FCSTD DOCUMENT  (FreeCAD 0.18R4 (GitTag))
Label: ZAntiWobbler
License: All rights reserved
LicenseURL: http://en.wikipedia.org/wiki/All_rights_reserved
objects: Sketcher::SketchObject×1, Spreadsheet::Sheet×1
note: 1 computed .brp shape members not serialized (recipe doc carries the construction recipe); baked Part::Feature solids carry a one-line shape summary decoded from their .brp

FEATURE [Sketcher::SketchObject] Sketch
  expr: Constraints[35] = Parameters.AntiWobblerRadius - Parameters.AntiWobblerRadiusToCut + 3mm
  expr: Constraints[34] = Parameters.AntiWobblerRadius * 2
  expr: Constraints[6] = Parameters.M3ThreadRadius
  expr: Constraints[14] = Parameters.M3ThreadRadius
  expr: Constraints[13] = Parameters.M3HeadRadius
  expr: Constraints[7] = Parameters.AntiWobblerRadiusToCut
  expr: Constraints[1] = Parameters.AntiWobblerRadius
  expr: Constraints[8] = Parameters.M3HeadRadius
  expr: Constraints[20] = Parameters.M3ThreadRadius
  expr: Constraints[15] = Parameters.AntiWobblerScrewSeparation
  expr: Constraints[10] = Parameters.M3HeadRadius
  expr: Constraints[5] = Parameters.M3HeadRadius
  expr: Constraints[2] = Parameters.ZScrewRadiusWithStopScrew
  expr: Constraints[11] = Parameters.M3ThreadRadius
  sketch-geometry (16):
    g0: Circle CenterX=0 CenterY=0 CenterZ=0 NormalX=0 NormalY=0 NormalZ=1 AngleXU=0 Radius=11
    g1: Circle CenterX=0 CenterY=0 CenterZ=0 NormalX=0 NormalY=0 NormalZ=1 AngleXU=0 Radius=5
    g2: Circle CenterX=5.65685 CenterY=5.65685 CenterZ=0 NormalX=0 NormalY=0 NormalZ=1 AngleXU=0 Radius=2
    g3: Circle CenterX=5.65685 CenterY=5.65685 CenterZ=0 NormalX=0 NormalY=0 NormalZ=1 AngleXU=0 Radius=3
    g4: Circle CenterX=5.65685 CenterY=-5.65685 CenterZ=0 NormalX=0 NormalY=0 NormalZ=1 AngleXU=0 Radius=3
    g5: Circle CenterX=-5.65685 CenterY=-5.65685 CenterZ=0 NormalX=0 NormalY=0 NormalZ=1 AngleXU=0 Radius=3
    g6: Circle CenterX=-5.65685 CenterY=-5.65685 CenterZ=0 NormalX=0 NormalY=0 NormalZ=1 AngleXU=0 Radius=2
    g7: Circle CenterX=-5.65685 CenterY=5.65685 CenterZ=0 NormalX=0 NormalY=0 NormalZ=1 AngleXU=0 Radius=3
    g8: Circle CenterX=-5.65685 CenterY=5.65685 CenterZ=0 NormalX=0 NormalY=0 NormalZ=1 AngleXU=0 Radius=2
    g9: LineSegment StartX=-7.55 StartY=11.0021 StartZ=0 EndX=-7.55 EndY=-10.9979 EndZ=0
    g10: Circle CenterX=5.65685 CenterY=-5.65685 CenterZ=0 NormalX=0 NormalY=0 NormalZ=1 AngleXU=0 Radius=2
    g11: LineSegment StartX=-14 StartY=-10.9979 StartZ=0 EndX=-7.55 EndY=-10.9979 EndZ=0
    g12: LineSegment StartX=-14 StartY=11.0021 StartZ=0 EndX=-14 EndY=-10.9979 EndZ=0
    g13: LineSegment StartX=-14 StartY=11.0021 StartZ=0 EndX=-7.55 EndY=11.0021 EndZ=0
    g14: LineSegment StartX=5.65685 StartY=5.65685 StartZ=0 EndX=-5.65685 EndY=-5.65685 EndZ=0
    g15: LineSegment StartX=-5.65685 StartY=5.65685 StartZ=0 EndX=5.65685 EndY=-5.65685 EndZ=0
  constraints (37):
    c: Coincident(g0,g-1)
    c: Radius(g0) = 11
    c: Radius(g1) = 5
    c: Coincident(g0,g1)
    c: Coincident(g2,g3)
    c: Radius(g3) = 3
    c: Radius(g2) = 2
    c: DistanceX(g9,g0) = 7.55
    c: Radius(g4) = 3
    c: Coincident(g8,g7)
    c: Radius(g7) = 3
    c: Radius(g8) = 2
    c: Coincident(g6,g5)
    c: Radius(g5) = 3
    c: Radius(g6) = 2
    c: Distance(g7,g4) = 16
    c: Symmetric(g2,g7,g-2)
    c: Symmetric(g4,g5,g-2)
    c: Symmetric(g2,g4,g-1)
    c: Vertical(g9)
    c: Radius(g10) = 2
    c: Coincident(g11,g9)
    c: Horizontal(g11)
    c: Coincident(g12,g11)
    c: Vertical(g12)
    c: Coincident(g13,g12)
    c: Coincident(g13,g9)
    c: Horizontal(g13)
    c: Coincident(g14,g2)
    c: Coincident(g14,g5)
    c: Coincident(g15,g7)
    c: Coincident(g15,g4)
    c: Perpendicular(g14,g15)
    c: Coincident(g10,g4)
    c: DistanceY(g11,g12) = 22
    c: DistanceX(g12,g9) = 6.45
    c: Distance(g9,g0) = 13.34
FEATURE [Spreadsheet::Sheet] Spreadsheet  label="Parameters"
  cells = A1=ZScrewRadiusWithStopScrew; B1(ZScrewRadiusWithStopScrew)=5; A2=M3ThreadRadius; B2(M3ThreadRadius)==2mm; A3=M3HeadRadius; B3(M3HeadRadius)==3mm; A4=M3HeadHeight; B4(M3HeadHeight)==4mm; A5=AntiWobblerHeight; B5(AntiWobblerHeight)==10mm; A6=AntiWobblerRadius; B6(AntiWobblerRadius)==11mm; A7=AntiWobblerRadiusToCut; B7(AntiWobblerRadiusToCut)==7.55mm; A8=AntiWobblerScrewSeparation; B8(AntiWobblerScrewSeparation)==16mm
